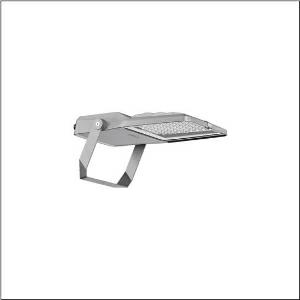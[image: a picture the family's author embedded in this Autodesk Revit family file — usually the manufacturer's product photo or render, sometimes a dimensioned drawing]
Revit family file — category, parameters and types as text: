
# Revit family: floodlight_fl_21_iq_mini___pl33t_5xa7772c2f1a_05f5
name_source: partatom
category: Lighting Fixtures
units: mm (PartAtom-declared; Revit-internal decimal feet)

## family parameters
Cut with Voids When Loaded = No
Host = Face
Light Source = No
Part Type = Normal
Room Calculation Point = No
Round Connector Dimension = Use Diameter
Shared = No

## types (1)
- --- (1 x LED, 12060 lm, 87.2 W, 3000K)
    Apparent Load = 87 VA
    CIE Flux Codes = 26 75 99 100 100
    Color Rendering = 70
    Color Temperature = 3000K
    Default Elevation = 1800 mm
    Description = Floodlight FL 21 iQ mini, floodlight, primary light control with lens, of PMMA, primary optical cover: protective disc, of toughened safety glass, transparent, light distribution: PL33T, light emission: direct distribution, installation type: surface-mounted, LED, High Power LED, rated luminous flux: 12.060lm, luminous efficacy: 138lm/W, light colour: 730, colour temperature: 3000K, control gear: iQ Street-Remote/DALI, control: Street-Remote, Auto-Match, Temp-Guard, Night-Set, Smart-Wire, Desk-Remote (wireless, voltage-free reading and setting of iQ features in the workshop via application-optimized NFC function/RFID function), optimised constant luminous flux control (CLO 2.0), with terminal, 6-pole, mains connection: 220..240V, AC, 50/60Hz, start of lifetime: 87W, end of service life: 92W, reduction: 40W, luminaire housing, of diecast aluminium, powder-coated, Siteco® metallic grey (DB 702S), corrosivity category C5 mid according to DIN EN ISO 12944, suitable for swimming pools, chlorine-resistant, sealing non-destructively replaceable, mounting bracket, of steel, galvanised, powder-coated, Siteco® metallic grey (DB 702S), protection rating (complete): IP66, insulation class (complete): insulation class II (safety insulation), certification: CE, ENEC, VDE, protection symbol: D, impact resistance: IK08, permissible operating ambient temperature: -40..+40°C, permissible operating ambient temperature for outdoor applications: -40..+50°C, standard: DIN EN 12944, LABS conformity tested according to VDMA 24364:2018-05, packaging unit: 1 piece

Light Distribution: PL33T
    Height = 70 mm
    Lamp = 1 x LED
    Lamp Light Flux = 12060 lm
    Lamp Power = 87.2 W
    Lamp count = 1
    Length = 485 mm
    Luminous efficacy = 138 lm/W
    Manufacturer = Siteco
    ModVariant = No
    Model = 5XA7772C2F1A
    Number of Poles = 1
    OnlyDefault = Yes
    Power Factor = 1
    Product Name = Floodlight FL 21 iQ mini | PL33T
    Product group = floodlight | pylon annexe
    ProductGroupID = 6200
    Protection Class = Protection class II
    Protection Degree = IP 66
    RLX_Detail_Level = 1
    RLX_Emergency_Light_Flux = 0 lm
    RLX_Emergency_Type = 0
    RLX_Emergency_Type_DB = No
    RlxData = <blob elided: 96217 chars, md5=3d3a50df>
    Socket = socket
    Standby Power = 0 W
    System Light Flux = 12060 lm
    System Power = 87 W
    Type Comments = factory setting: luminous flux: 100 % | dim-lin: 254 | 456 mA
    Type Image = l_1006845.jpg
    URL = http://relux.com
    VarID = @adj_149564
    Voltage = 0 V
    Weight = 0.00 kg
    Width = 337 mm

## geometry (parser evidence)
native form markers: Blend x4, Sweep x13
no freeform markers — native parametric forms only
